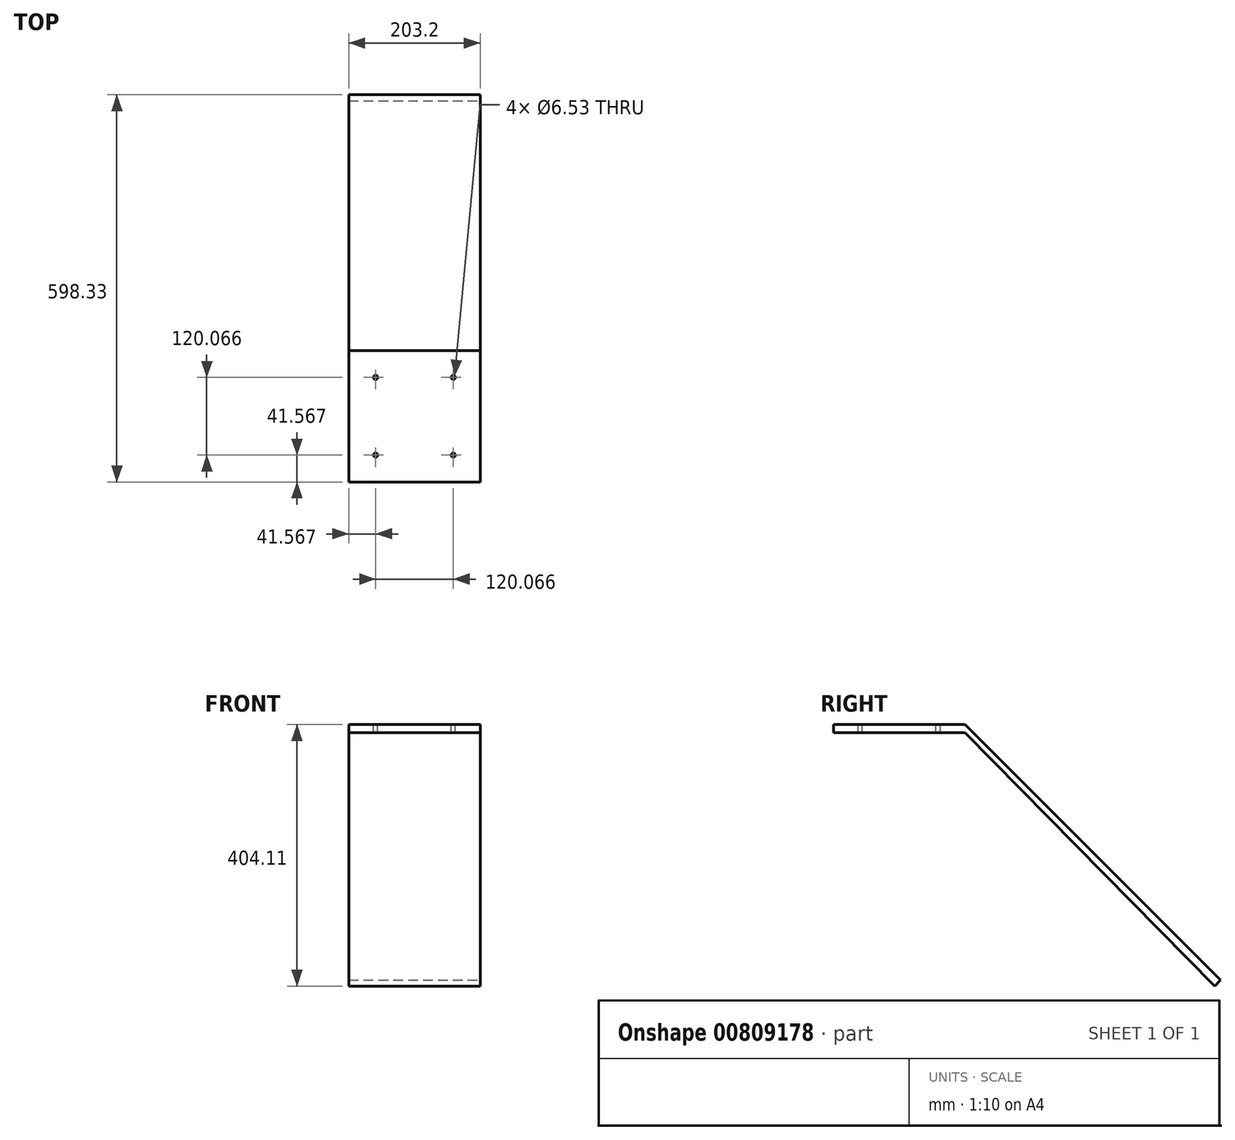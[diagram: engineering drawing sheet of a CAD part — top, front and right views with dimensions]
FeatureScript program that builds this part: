
annotation { "Feature Type Name" : "Feature", "Feature Type Description" : "" }
export const myFeature = defineFeature(function(context is Context, id is Id, definition is map)
    precondition{}
    {
        {
            var Q0;
            Q0=qCreatedBy(makeId("Right.planeOp"),FACE);
            var sketch = newSketch(context, id + "F0", { "sketchPlane" : qUnion([Q0])});
            skLineSegment(sketch, "E0", {"start": v(0, 0) * mm, "end": v(203.2, 0) * mm});
            skLineSegment(sketch, "E1", {"start": v(203.2, 0) * mm, "end": v(598.33, -395.13) * mm});
            skLineSegment(sketch, "E2", {"start": v(0, 0) * mm, "end": v(0, -12.7) * mm});
            skLineSegment(sketch, "E3", {"start": v(0, -12.7) * mm, "end": v(203.2, -12.7) * mm});
            skLineSegment(sketch, "E4", {"start": v(203.2, -12.7) * mm, "end": v(203.2, 0) * mm});
            skLineSegment(sketch, "E5", {"start": v(203.2, -12.7) * mm, "end": v(589.35, -404.11) * mm});
            skLineSegment(sketch, "E6", {"start": v(589.35, -404.11) * mm, "end": v(598.33, -395.13) * mm});
            skSolve(sketch);
        }
        {
            var Q0;
            Q0 = qSketchRegion(id + "F0", true);
            extrude(context, id + "F1", {"entities" : qUnion([Q0]), "oppositeDirection" : true, "depth" : 203.2 * mm, "offsetDistance" : 25.4 * mm});
        }
        {
            var Q0;
            Q0=makeQuery(id+"F1.opExtrude","SWEPT_FACE",FACE,{"disambiguationData":[OSD([sQuery(id+"F0.wireOp",EDGE,"E0")])]});
            var sketch = newSketch(context, id + "F2", { "sketchPlane" : qUnion([Q0])});
            skPoint(sketch, "E7", {"position": v(-101.6, 101.6) * mm});
            skPoint(sketch, "E8", {"position": v(-41.57, 41.57) * mm});
            skCircle(sketch, "E9", {"center": v(-101.6, 101.6) * mm, "radius": 85 * mm});
            skLineSegment(sketch, "E10", {"start": v(-101.6, 101.6) * mm, "end": v(-16.6, 101.6) * mm});
            skLineSegment(sketch, "E11", {"start": v(-101.6, 101.6) * mm, "end": v(-41.57, 41.57) * mm});
            skPoint(sketch, "E12.1.0", {"position": v(-41.57, 161.63) * mm});
            skPoint(sketch, "E12.2.0", {"position": v(-161.63, 161.63) * mm});
            skPoint(sketch, "E12.3.0", {"position": v(-161.63, 41.57) * mm});
            skSolve(sketch);
        }
        {
            var Q0;
            Q0=sQuery(id+"F2.wireOp",VERTEX,"E12.2.0");
            var Q1;
            Q1=sQuery(id+"F2.wireOp",VERTEX,"E12.3.0");
            var Q2;
            Q2=sQuery(id+"F2.wireOp",VERTEX,"E8");
            var Q3;
            Q3=sQuery(id+"F2.wireOp",VERTEX,"E12.1.0");
            var Q4;
            Q4=makeQuery(id+"F1.opExtrude","SWEPT_BODY",BODY,{"disambiguationData":[OSD([sQuery(id+"F0.wireOp",EDGE,"E0"),sQuery(id+"F0.wireOp",EDGE,"E1"),sQuery(id+"F0.wireOp",EDGE,"E2"),sQuery(id+"F0.wireOp",EDGE,"E3"),sQuery(id+"F0.wireOp",EDGE,"E5"),sQuery(id+"F0.wireOp",EDGE,"E6")])]});
            hole(context, id + "F3", {"style" : HoleStyle.SIMPLE, "endStyle" : HoleEndStyle.THROUGH, "standardTappedOrClearance" : lookupTablePath({ "standard" : "ANSI", "engagement" : "75%", "pitch" : "18 tpi", "size" : "5/16", "type" : "Tapped" }), "standardBlindInLast" : lookupTablePath({ "standard" : "ANSI", "engagement" : "75%", "pitch" : "18 tpi", "size" : "5/16", "type" : "Tapped" }), "holeDiameter" : 6.53 * mm, "majorDiameter" : 7.94 * mm, "showTappedDepth" : true, "isTappedThrough" : true, "tappedDepth" : 12.7 * mm, "tapClearance" : 3, "locations" : qUnion([Q0, Q1, Q2, Q3]), "scope" : qUnion([Q4])});
        }
    });
